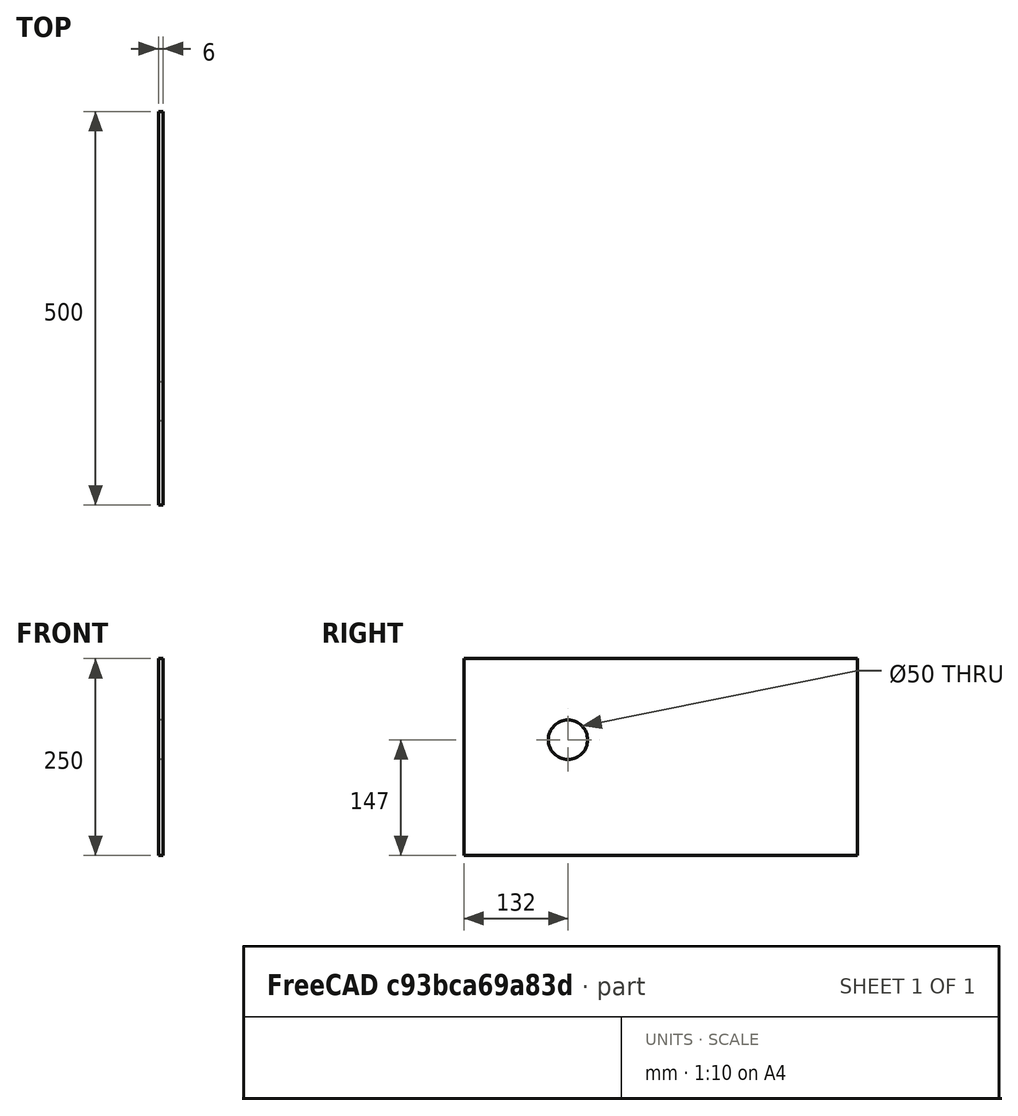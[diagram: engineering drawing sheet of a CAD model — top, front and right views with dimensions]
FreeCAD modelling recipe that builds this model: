
FCSTD DOCUMENT  (FreeCAD 0.18R4 (GitTag))
Label: Gabinete_Lateral2
License: All rights reserved
LicenseURL: http://en.wikipedia.org/wiki/All_rights_reserved
objects: Sketcher::SketchObject×1, PartDesign::Pad×1, PartDesign::Body×1
note: 4 computed .brp shape members not serialized (recipe doc carries the construction recipe); baked Part::Feature solids carry a one-line shape summary decoded from their .brp

FEATURE [Sketcher::SketchObject] Sketch
  MapMode = 5
  Placement = pos=(0,0,0) rot=(0.57735,0.57735,0.57735;2.0944rad)
  Support = -> [YZ_Plane]
  sketch-geometry (5):
    g0: LineSegment StartX=0 StartY=0 StartZ=0 EndX=500 EndY=0 EndZ=0
    g1: LineSegment StartX=500 StartY=0 StartZ=0 EndX=500 EndY=250 EndZ=0
    g2: LineSegment StartX=500 StartY=250 StartZ=0 EndX=0 EndY=250 EndZ=0
    g3: LineSegment StartX=0 StartY=250 StartZ=0 EndX=0 EndY=0 EndZ=0
    g4: Circle CenterX=132 CenterY=147 CenterZ=0 NormalX=0 NormalY=0 NormalZ=1 AngleXU=0 Radius=25
  constraints (14):
    c: Coincident(g0,g1)
    c: Coincident(g1,g2)
    c: Coincident(g2,g3)
    c: Coincident(g3,g0)
    c: Horizontal(g0)
    c: Horizontal(g2)
    c: Vertical(g1)
    c: Vertical(g3)
    c: Coincident(g0,g-1)
    c: DistanceX(g0,g0) = 500
    c: DistanceY(g3,g3) = 250
    c: Radius(g4) = 25
    c: Distance(g4,g0) = 147
    c: Distance(g4,g3) = 132
FEATURE [PartDesign::Pad] Pad
  Length = 6
  Length2 = 100
  Placement = pos=(0,0,0) rot=(0.57735,0.57735,0.57735;2.0944rad)
  Profile = -> Sketch
  Type = 0
FEATURE [PartDesign::Body] Body
  Group = -> [Sketch,Pad]
  Origin = -> Origin
  Tip = -> Pad
